# Revit family: Pump_Commercial-Submersible-Zoeller-Aqua_Mate-72_Series
name_source: partatom
category: Mechanical Equipment
revit_build: Autodesk Revit 2014 (Build: 20130308_1515(x64)
units: mm (PartAtom-declared; Revit-internal decimal feet)

## types (1)
- M72
    Amps = 3 A
    Apparent Load = 357 VA
    Cooling = Oil free
    Cord Length = 9' standard
    Cord Type = UL listed, 3-wire, grounded plug
    Default Elevation = 0"
    Description = Submersible pump for dewatering.
    Discharge Diameter = 1-1/2" NPT
    Discharge Height = 3 3/4"
    Discharge Radius = 3/4"
    Flow @ 5' = 38 GPM
    Hertz = 60
    Impeller = Engineered plastic
    Impeller Type = Non-clogging vortex
    Installation Type = Floor Mounted
    Insulation = Class B
    Length = 7 1/8"
    Manufacturer = Zoeller
    Material = Cast Iron-Zoeller-Powder Coated Epoxy
    Max. Operating Temp. = 110° F
    Maximum Head = 18 ft.
    Mechanical Seals = Carbon and ceramic
    Model = 72
    Motor = 3/10 HP
    Motor Protection = Auto reset thermal overload
    Off Point = 3.625
    On Point = 7.375
    Operation = Automatic
    Overall Height = 11 13/16"
    Phase = 1 Ph
    Price = Prices may vary. Please consult Manufacturer Representative for most up-to-date price list.
    Product Page URL = http://www.zoellerpumps.com
    RPM = 3400
    Solid Handling = 3/8" spherical solids
    Type = Permanent Split Capacitor
    URL = http://www.zoellerpumps.com
    Voltage = 115 V
    Warranty Information = 36 Months (Limited)
    Waste Connection = Yes
    Width = 9 1/16"

## geometry (parser evidence)
native form markers: Sweep x3
no freeform markers — native parametric forms only
